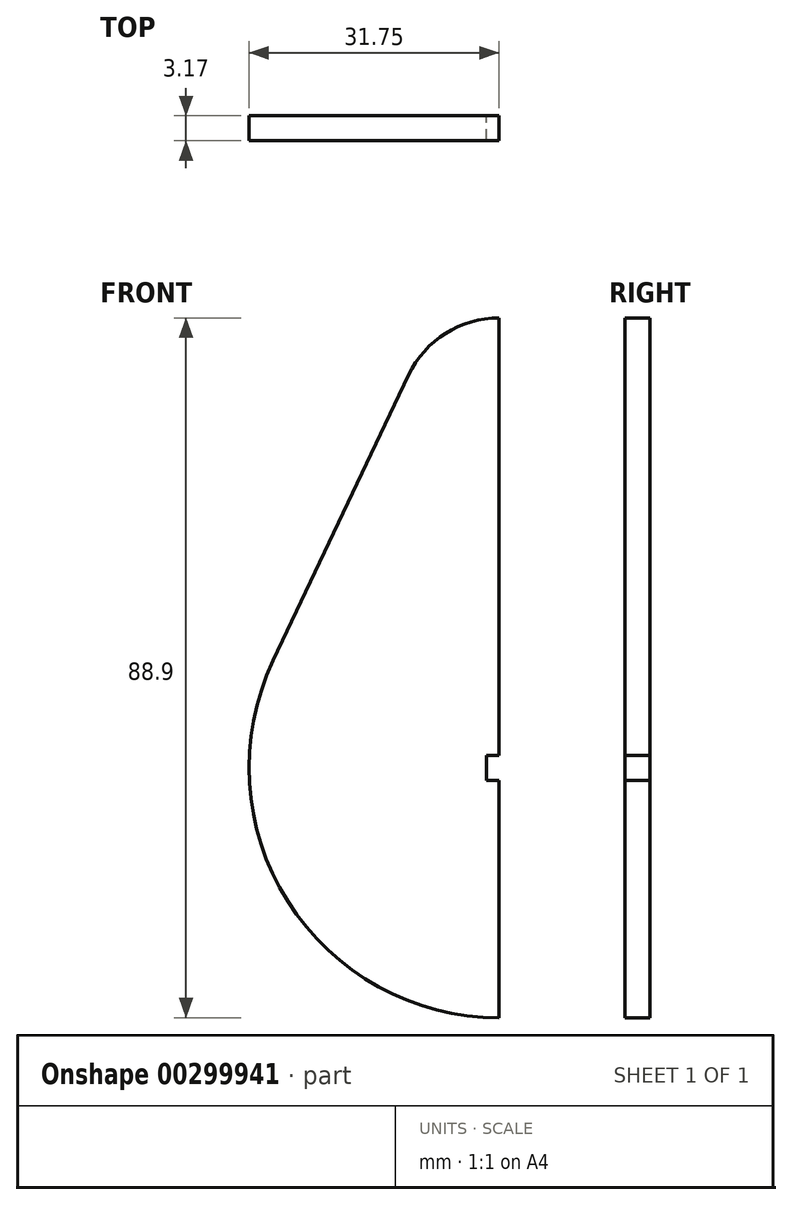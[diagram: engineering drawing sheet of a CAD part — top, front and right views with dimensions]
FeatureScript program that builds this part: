
annotation { "Feature Type Name" : "Feature", "Feature Type Description" : "" }
export const myFeature = defineFeature(function(context is Context, id is Id, definition is map)
    precondition{}
    {
        {
            var Q0;
            Q0=qCreatedBy(makeId("Front.planeOp"),FACE);
            var sketch = newSketch(context, id + "F0", { "sketchPlane" : qUnion([Q0])});
            skLineSegment(sketch, "E0", {"start": v(0, 0) * mm, "end": v(0, 44.45) * mm});
            skArc(sketch, "E1", {"start": v(0, 57.15) * mm, "mid": v(6.79, 55.18) * mm, "end": v(11.47, 49.9) * mm});
            skArc(sketch, "E2", {"start": v(0, -31.75) * mm, "mid": v(26.83, -16.97) * mm, "end": v(28.69, 13.6) * mm});
            skLineSegment(sketch, "E3", {"start": v(11.47, 49.9) * mm, "end": v(28.69, 13.6) * mm});
            skPoint(sketch, "E4.orphan", {"position": v(12.7, 44.45) * mm});
            skLineSegment(sketch, "E5", {"start": v(0, 57.15) * mm, "end": v(0, -31.75) * mm});
            skArc(sketch, "E6.MirrorCS", {"start": v(0, 57.15) * mm, "mid": v(-6.79, 55.18) * mm, "end": v(-11.47, 49.9) * mm});
            skLineSegment(sketch, "E7.MirrorCS", {"start": v(-11.47, 49.9) * mm, "end": v(-28.69, 13.6) * mm});
            skArc(sketch, "E8.MirrorCS", {"start": v(0, -31.75) * mm, "mid": v(-26.83, -16.97) * mm, "end": v(-28.69, 13.6) * mm});
            skLineSegment(sketch, "E9.bottom", {"start": v(1.59, 1.59) * mm, "end": v(-1.59, 1.59) * mm});
            skLineSegment(sketch, "E9.top", {"start": v(1.59, -1.59) * mm, "end": v(-1.59, -1.59) * mm});
            skLineSegment(sketch, "E9.left", {"start": v(1.59, 1.59) * mm, "end": v(1.59, -1.59) * mm});
            skLineSegment(sketch, "E9.right", {"start": v(-1.59, 1.59) * mm, "end": v(-1.59, -1.59) * mm});
            skSolve(sketch);
        }
        {
            var Q0;
            {var subQ7=sQuery(id+"F0.wireOp",EDGE,"E6.MirrorCS");Q0=makeQuery(id+"F0.imprint","IMPRINT",FACE,{"disambiguationData":[TD([[makeQuery(id+"F0.imprint","IMPRINT",EDGE,{"derivedFrom":subQ7}),1.0]])]});}
            var Q1;
            {var subQ1=sQuery(id+"F0.wireOp",EDGE,"E1");Q1=makeQuery(id+"F0.imprint","IMPRINT",FACE,{"disambiguationData":[TD([[makeQuery(id+"F0.imprint","IMPRINT",EDGE,{"derivedFrom":subQ1}),-1.0]])]});}
            extrude(context, id + "F1", {"entities" : qUnion([Q0, Q1]), "depth" : 3.17 * mm});
        }
    });
